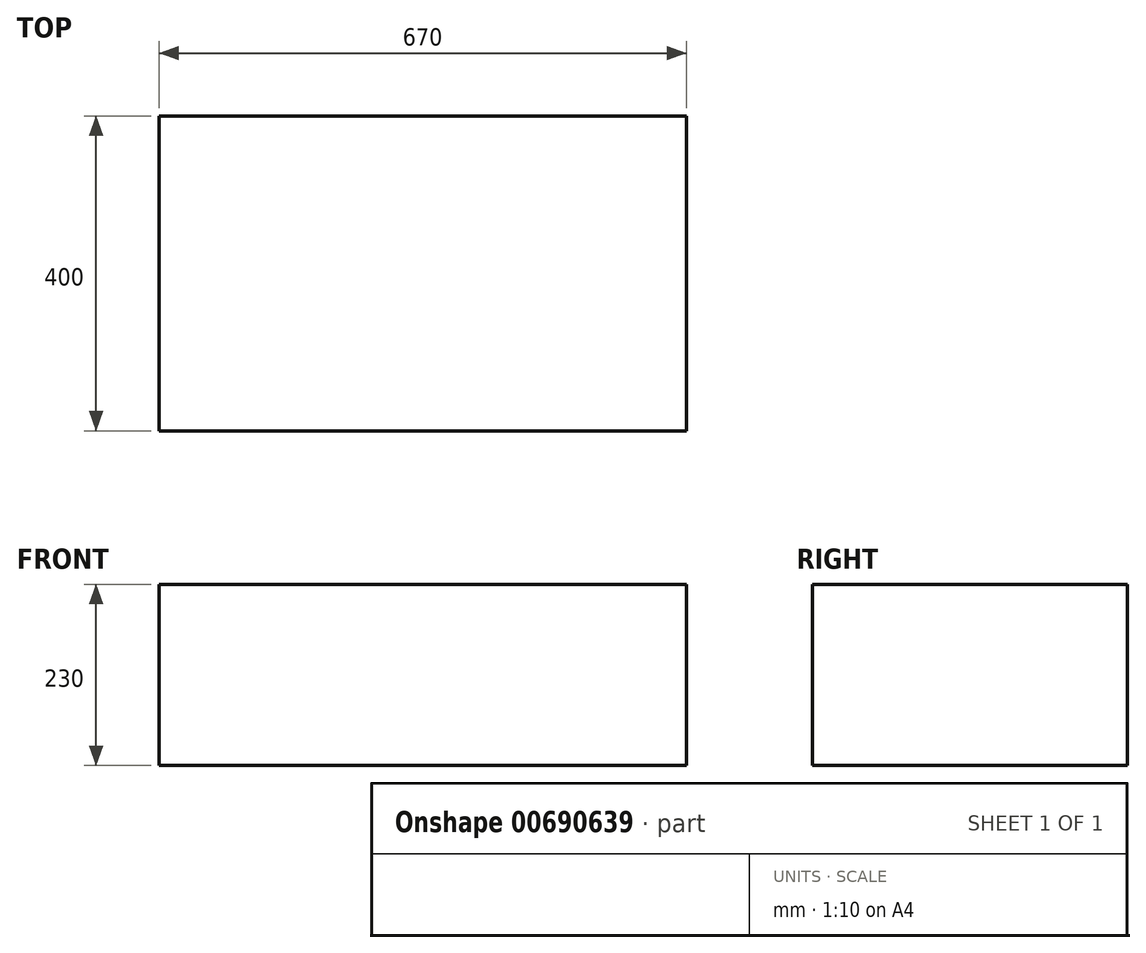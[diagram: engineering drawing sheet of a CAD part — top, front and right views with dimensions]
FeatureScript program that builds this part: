
annotation { "Feature Type Name" : "Feature", "Feature Type Description" : "" }
export const myFeature = defineFeature(function(context is Context, id is Id, definition is map)
    precondition{}
    {
        {
            var Q0;
            Q0=qCreatedBy(makeId("Top.planeOp"),FACE);
            var sketch = newSketch(context, id + "F0", { "sketchPlane" : qUnion([Q0])});
            skLineSegment(sketch, "E0", {"start": v(-335, 0) * mm, "end": v(335, 0) * mm});
            skLineSegment(sketch, "E1", {"start": v(335, 0) * mm, "end": v(335, 400) * mm});
            skLineSegment(sketch, "E2", {"start": v(335, 400) * mm, "end": v(-335, 400) * mm});
            skLineSegment(sketch, "E3", {"start": v(-335, 400) * mm, "end": v(-335, 0) * mm});
            skSolve(sketch);
        }
        {
            var Q0;
            Q0=makeQuery(id+"F0.imprint","IMPRINT",FACE,{"disambiguationData":[TD([[makeQuery(id+"F0.imprint","IMPRINT",EDGE,{"derivedFrom":sQuery(id+"F0.wireOp",EDGE,"E0")}),1.0]])]});
            extrude(context, id + "F1", {"entities" : qUnion([Q0]), "depth" : 230 * mm, "offsetDistance" : 25 * mm});
        }
        {
            var Q0;
            Q0=makeQuery(id+"F0.imprint","IMPRINT",FACE,{"disambiguationData":[TD([[makeQuery(id+"F0.imprint","IMPRINT",EDGE,{"derivedFrom":sQuery(id+"F0.wireOp",EDGE,"E0")}),1.0]])]});
            extrude(context, id + "F2", {"entities" : qUnion([Q0]), "depth" : 230 * mm, "offsetDistance" : 25 * mm});
        }
        {
            var Q0;
            Q0=makeQuery(id+"F2.opExtrude","SWEPT_BODY",BODY,{"disambiguationData":[OSD([sQuery(id+"F0.wireOp",EDGE,"E0"),sQuery(id+"F0.wireOp",EDGE,"E1"),sQuery(id+"F0.wireOp",EDGE,"E2"),sQuery(id+"F0.wireOp",EDGE,"E3")])]});
            deleteBodies(context, id + "F3", {"entities" : qUnion([Q0])});
        }
    });
